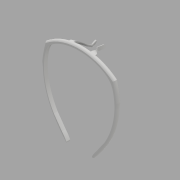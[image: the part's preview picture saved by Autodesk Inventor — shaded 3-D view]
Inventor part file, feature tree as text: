
AUTODESK INVENTOR PART (.ipt)
format: ipt  version: 2017 (Build 210142000, 142)  size: 3,570,176 bytes
history: native  units: mm
features: sketch x12, projected_geometry x6, plane x5, extrude x4, other x4, fillet x3, mirror x2, sweep x1, loft x1
ambient origin geometry x8: Origin, YZ Plane, XZ Plane, XY Plane, X Axis, Y Axis, Z Axis, Center Point
bodies: Solid1 (feature_tree)
feature tree (38):
  extrude  "Extrusion1"  Depth=121.5mm
  sketch  "Sketch2"  dims[d2=50.0mm d3=50.0mm]
  sweep  "Sweep1"
  extrude  "Extrusion2"  Depth=16.2mm
  mirror  "Mirror2"
  fillet  "Fillet1"  Radius=100.0mm
  plane  "Work Plane1"
  sketch  "Sketch5"  dims[d8=31.5mm d9=44.5mm]
  sketch  "Sketch6"  dims[d10=2.8mm d12=4.9mm]
  extrude  "Extrusion5"  Depth=44.5mm
  plane  "Work Plane2"
  sketch  "Sketch8"  dims[d19=3.4mm]
  sketch  "Sketch9"  dims[d20=3.0mm]
  plane  "Work Plane3"
  sketch  "Sketch10"  dims[d21=14.0mm]
  plane  "Work Plane4"
  loft  "Loft2"
  plane  "Work Plane5"
  extrude  "Extrusion6"  Depth=4.8mm
  fillet  "Fillet3"  Radius=8.0mm
  mirror  "Mirror3"
  fillet  "Fillet4"  Radius=32.0mm
  other  "bottom_view"
  sketch  "Sketch1"  dims[d0=120.0mm d1=121.5mm]
  projected_geometry  "Projected Loop4"
  sketch  "3D Sketch1"
  sketch  "Sketch4"  dims[d4=88.0mm d6=16.2mm d7=100.0mm]
  projected_geometry  "Projected Loop5"
  projected_geometry  "Projected Loop6"
  other  "Image1"
  other  "Image2"
  sketch  "Sketch7"  dims[d15=3.6mm d16=4.8mm d17=8.0mm d18=32.0mm]
  projected_geometry  "Projected Loop8"
  projected_geometry  "Projected Loop9"
  projected_geometry  "Projected Loop10"
  sketch  "Sketch11"  dims[d22=4.3mm]
  sketch  "Sketch12"  dims[d23=3.4mm d24=3.4mm d27=0.1mm d28=4.8mm d29=7.2mm d30=0.0mm d32=4.9mm d33=2.0mm d34=0.0mm d35=0.0mm d36=10.0mm d37=0.0mm d38=1.0mm d39=30.7mm d40=10.7mm d41=6.7mm d42=6.0mm d52=96.0mm d86=22.0mm d87=9.0mm d89=11.487737mm d129=140.0mm d172=68.052405mm d186=4.6mm d187=4.0mm d188=8.0mm d198=4.0mm d199=0.0mm d200=9.5mm d201=45.0deg d202=2.0mm d203=3.9mm d204=44.0mm d205=12.0mm d210=-27.5mm d211=2.0mm d212=3.6mm d213=8.0mm d214=5.0mm d215=2.094395mm d216=-20.5mm d217=1.5mm d218=3.75mm d219=30.0deg d220=9.0mm d221=10.5mm d222=10.0mm d223=90.0deg d224=0.0mm d225=90.0deg d226=0.0mm d227=90.0deg d228=10.0mm d229=90.0deg d231=75.0deg d232=2.0mm d233=0.0mm d234=1.0mm d235=1.5mm d237=342.0mm d266=0.174533mm]
  other  "Image3"
